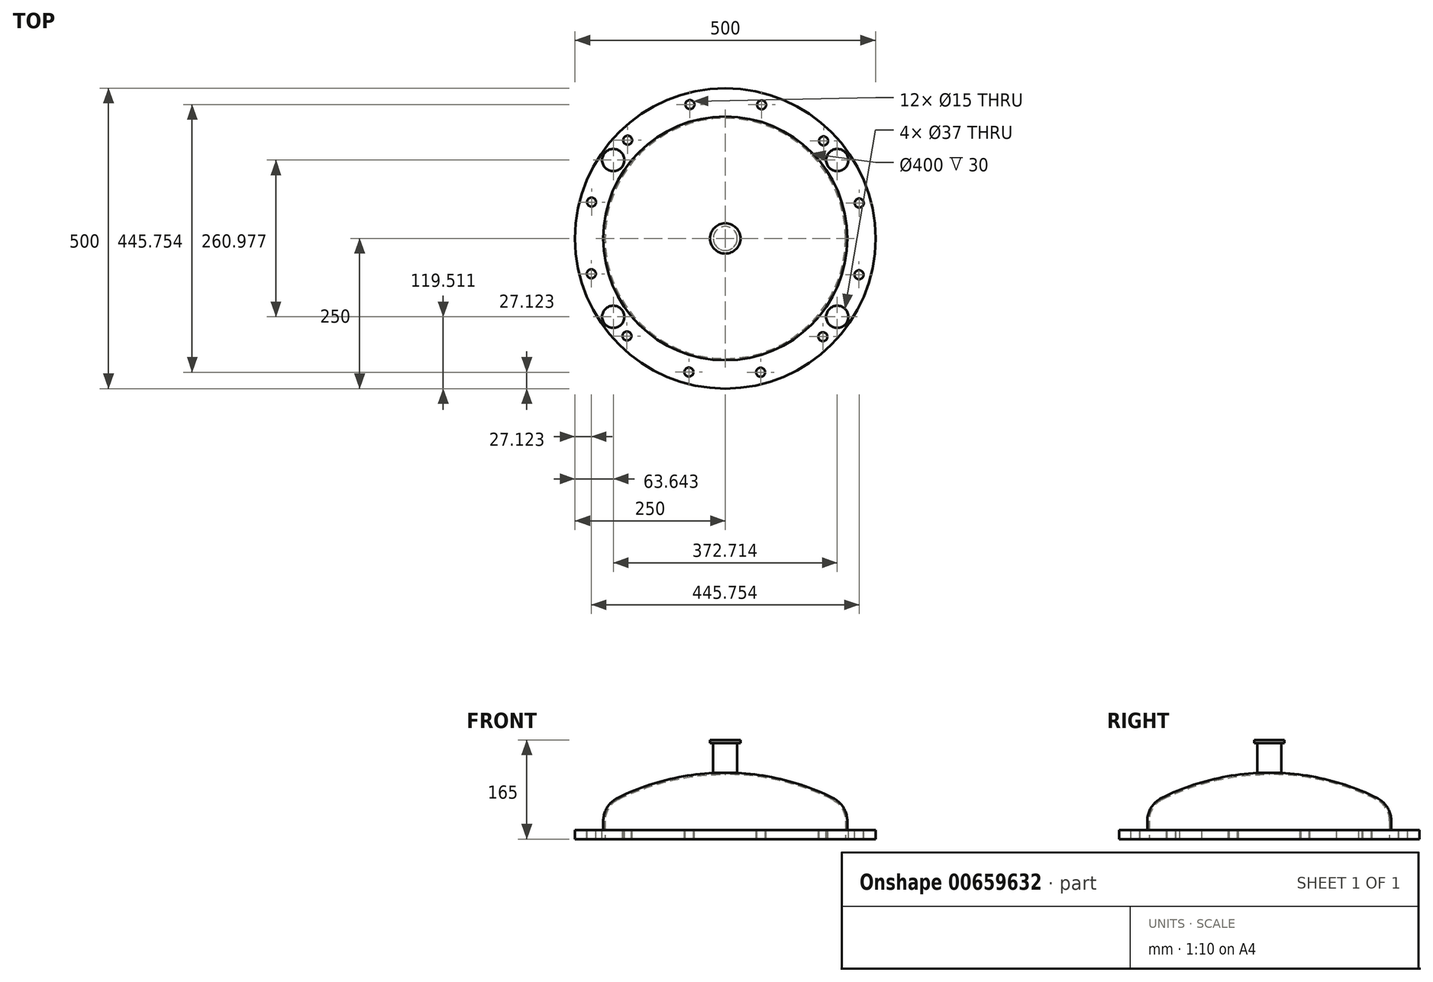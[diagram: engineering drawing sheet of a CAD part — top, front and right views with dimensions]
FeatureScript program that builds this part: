
annotation { "Feature Type Name" : "Feature", "Feature Type Description" : "" }
export const myFeature = defineFeature(function(context is Context, id is Id, definition is map)
    precondition{}
    {
        {
            var Q0;
            Q0=qCreatedBy(makeId("Front.planeOp"),FACE);
            var sketch = newSketch(context, id + "F0", { "sketchPlane" : qUnion([Q0])});
            skLineSegment(sketch, "E0", {"start": v(200, 0) * mm, "end": v(203, 0) * mm});
            skLineSegment(sketch, "E1", {"start": v(203, 0) * mm, "end": v(203, 20) * mm});
            skLineSegment(sketch, "E2", {"start": v(200, 0) * mm, "end": v(200, 20) * mm});
            skArc(sketch, "E3", {"start": v(200, 20) * mm, "mid": v(194, 41.07) * mm, "end": v(177.8, 55.82) * mm});
            skArc(sketch, "E4", {"start": v(177.8, 55.82) * mm, "mid": v(91.32, 87) * mm, "end": v(0, 97.6) * mm});
            skArc(sketch, "E5.0", {"start": v(179.13, 58.5) * mm, "mid": v(92, 89.92) * mm, "end": v(0, 100.6) * mm});
            skArc(sketch, "E5.1", {"start": v(203, 20) * mm, "mid": v(196.55, 42.65) * mm, "end": v(179.13, 58.5) * mm});
            skLineSegment(sketch, "E6", {"start": v(0, 97.6) * mm, "end": v(0, 100.6) * mm});
            skSolve(sketch);
        }
        {
            var Q0;
            Q0=qSketchRegion(id+"F0",true);
            var Q1;
            Q1=sQuery(id+"F0.wireOp",EDGE,"E6");
            revolve(context, id + "F1", {"entities" : qUnion([Q0]), "axis" : qUnion([Q1]), "revolveType" : RevolveType.FULL});
        }
        {
            var Q0;
            Q0=makeQuery(id+"F1.opRevolve","SWEPT_FACE",FACE,{"disambiguationData":[OSD([sQuery(id+"F0.wireOp",EDGE,"E0")])]});
            var sketch = newSketch(context, id + "F2", { "sketchPlane" : qUnion([Q0])});
            skCircle(sketch, "E7", {"center": v(0, 0) * mm, "radius": 250 * mm});
            skCircle(sketch, "E8", {"center": v(0, 0) * mm, "radius": 200 * mm});
            skSolve(sketch);
        }
        {
            var Q0;
            Q0=qSketchRegion(id+"F2",true);
            extrude(context, id + "F3", {"entities" : qUnion([Q0]), "operationType" : NewBodyOperationType.ADD, "depth" : 10 * mm, "offsetDistance" : 25 * mm, "hasSecondDirection" : true, "secondDirectionOppositeDirection" : true, "secondDirectionDepth" : 5 * mm});
        }
        {
            var Q0;
            Q0=makeQuery(id+"F3.opExtrude","CAP_FACE",FACE,{"disambiguationData":[OSD([sQuery(id+"F2.wireOp",EDGE,"E7"),sQuery(id+"F2.wireOp",EDGE,"E8")])],"isStart":true});
            var sketch = newSketch(context, id + "F4", { "sketchPlane" : qUnion([Q0])});
            skCircle(sketch, "E9", {"center": v(222.88, 58.88) * mm, "radius": 7.5 * mm});
            skLineSegment(sketch, "E10", {"start": v(222.88, 58.88) * mm, "end": v(3.13, 0) * mm, "construction": true});
            skLineSegment(sketch, "E11", {"start": v(3.13, 0) * mm, "end": v(170.3, 0) * mm, "construction": true});
            skCircle(sketch, "E12.1.0", {"center": v(163.58, 162.43) * mm, "radius": 7.5 * mm});
            skCircle(sketch, "E12.2.0", {"center": v(60.45, 222.46) * mm, "radius": 7.5 * mm});
            skCircle(sketch, "E12.3.0", {"center": v(-58.88, 222.88) * mm, "radius": 7.5 * mm});
            skCircle(sketch, "E12.4.0", {"center": v(-162.43, 163.58) * mm, "radius": 7.5 * mm});
            skCircle(sketch, "E12.5.0", {"center": v(-222.46, 60.45) * mm, "radius": 7.5 * mm});
            skCircle(sketch, "E12.6.0", {"center": v(-222.88, -58.88) * mm, "radius": 7.5 * mm});
            skCircle(sketch, "E12.7.0", {"center": v(-163.58, -162.43) * mm, "radius": 7.5 * mm});
            skCircle(sketch, "E12.8.0", {"center": v(-60.45, -222.46) * mm, "radius": 7.5 * mm});
            skCircle(sketch, "E12.9.0", {"center": v(58.88, -222.88) * mm, "radius": 7.5 * mm});
            skCircle(sketch, "E12.10.0", {"center": v(162.43, -163.58) * mm, "radius": 7.5 * mm});
            skCircle(sketch, "E12.11.0", {"center": v(222.46, -60.45) * mm, "radius": 7.5 * mm});
            skPoint(sketch, "E12.center", {"position": v(0, 0) * mm});
            skSolve(sketch);
        }
        {
            var Q0;
            Q0=qSketchRegion(id+"F4",true);
            extrude(context, id + "F5", {"entities" : qUnion([Q0]), "operationType" : NewBodyOperationType.REMOVE, "endBound" : BoundingType.UP_TO_NEXT, "oppositeDirection" : true, "depth" : 25 * mm, "offsetDistance" : 25 * mm});
        }
        {
            var Q0;
            Q0=qCreatedBy(makeId("Top.planeOp"),FACE);
            cPlane(context, id + "F6", {"entities" : qUnion([Q0]), "cplaneType" : CPlaneType.OFFSET, "offset" : 150 * mm, "width" : 150 * mm, "height" : 150 * mm});
        }
        {
            var Q0;
            Q0=qCreatedBy(id+"F6.planeOp",FACE);
            var sketch = newSketch(context, id + "F7", { "sketchPlane" : qUnion([Q0])});
            skCircle(sketch, "E13", {"center": v(0, 0) * mm, "radius": 20 * mm});
            skSolve(sketch);
        }
        {
            var Q0;
            Q0=qSketchRegion(id+"F7",true);
            extrude(context, id + "F8", {"entities" : qUnion([Q0]), "operationType" : NewBodyOperationType.ADD, "endBound" : BoundingType.UP_TO_NEXT, "oppositeDirection" : true, "depth" : 25 * mm, "offsetDistance" : 25 * mm});
        }
        {
            var Q0;
            Q0=makeQuery(id+"F8.opExtrude","CAP_FACE",FACE,{"disambiguationData":[OSD([sQuery(id+"F7.wireOp",EDGE,"E13")])],"isStart":true});
            var sketch = newSketch(context, id + "F9", { "sketchPlane" : qUnion([Q0])});
            skCircle(sketch, "E14", {"center": v(0, 0) * mm, "radius": 25.25 * mm});
            skSolve(sketch);
        }
        {
            var Q0;
            Q0=qSketchRegion(id+"F9",true);
            extrude(context, id + "F10", {"entities" : qUnion([Q0]), "operationType" : NewBodyOperationType.ADD, "depth" : 5 * mm, "offsetDistance" : 25 * mm});
        }
        {
            var Q0;
            Q0=makeQuery(id+"F3.opExtrude","CAP_FACE",FACE,{"disambiguationData":[OSD([sQuery(id+"F2.wireOp",EDGE,"E7"),sQuery(id+"F2.wireOp",EDGE,"E8")])],"isStart":true});
            var sketch = newSketch(context, id + "F11", { "sketchPlane" : qUnion([Q0])});
            skCircle(sketch, "E15", {"center": v(186.36, 130.49) * mm, "radius": 18.5 * mm});
            skLineSegment(sketch, "E16", {"start": v(0, 0) * mm, "end": v(186.36, 130.49) * mm, "construction": true});
            skLineSegment(sketch, "E17", {"start": v(0, 0) * mm, "end": v(153.35, 0) * mm, "construction": true});
            skCircle(sketch, "E18.MirrorC", {"center": v(-186.36, 130.49) * mm, "radius": 18.5 * mm});
            skLineSegment(sketch, "E19.MirrorCS", {"start": v(0, 0) * mm, "end": v(-186.36, 130.49) * mm, "construction": true});
            skCircle(sketch, "E20.MirrorC", {"center": v(-186.36, -130.49) * mm, "radius": 18.5 * mm});
            skCircle(sketch, "E21.MirrorC", {"center": v(186.36, -130.49) * mm, "radius": 18.5 * mm});
            skLineSegment(sketch, "E22.MirrorCS", {"start": v(0, 0) * mm, "end": v(186.36, -130.49) * mm, "construction": true});
            skSolve(sketch);
        }
        {
            var Q0;
            Q0 = qSketchRegion(id + "F11", true);
            extrude(context, id + "F12", {"entities" : qUnion([Q0]), "operationType" : NewBodyOperationType.REMOVE, "oppositeDirection" : true, "depth" : 20 * mm, "offsetDistance" : 25 * mm});
        }
    });
